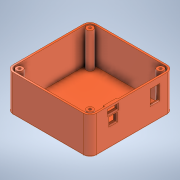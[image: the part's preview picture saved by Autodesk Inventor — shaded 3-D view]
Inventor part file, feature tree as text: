
AUTODESK INVENTOR PART (.ipt)
format: ipt  version: 2020 (Build 240168000, 168)  size: 254,464 bytes
history: native  units: in
note: dims shown in document units (in); Inventor stores cm internally (conversion verified against a paired STEP export)
features: extrude x6, sketch x6, projected_geometry x5, mirror x2, chamfer x2, shell x1, fillet x1
ambient origin geometry x8: Origin, YZ Plane, XZ Plane, XY Plane, X Axis, Y Axis, Z Axis, Center Point
bodies: Solid1 (feature_tree)
feature tree (23):
  extrude  "Extrusion1"  Depth=3.1496in
  shell  "Shell1"  Thickness=0.25in
  fillet  "Fillet1"  Radius=1.0in
  extrude  "Extrusion2"  Depth=0.05in
  mirror  "Mirror1"
  mirror  "Mirror2"
  extrude  "Extrusion4"  Depth=0.25in
  extrude  "Extrusion5"  Depth=0.3937in TaperAngle=0.0deg
  extrude  "Extrusion6"  Depth=0.5in
  chamfer  "Chamfer1"  Distance=0.3937in
  extrude  "Extrusion7"  Depth=0.1575in
  chamfer  "Chamfer2"  Distance=0.0689in
  sketch  "Sketch1"  dims[d0=3.1496in d1=3.1496in d2=0.25in d3=1.0in d4=0.0in]
  sketch  "Sketch2"  dims[d5=0.0669in d6=0.05in]
  sketch  "Sketch4"  dims[d7=0.25in d8=0.0945in]
  projected_geometry  "Projected Loop1"
  projected_geometry  "Projected Loop2"
  projected_geometry  "Projected Loop3"
  projected_geometry  "Projected Loop4"
  projected_geometry  "Projected Loop5"
  sketch  "Sketch5"  dims[d9=1.0in d10=0.0in d16=0.3937in d17=0.0in]
  sketch  "Sketch6"  dims[d18=0.05in d19=0.5in d20=0.3937in d21=0.0in]
  sketch  "Sketch7"  dims[d22=0.3543in d23=0.1575in d24=0.0689in d25=0.1181in d26=0.252in d27=0.252in d28=0.1181in d29=0.3937in d30=0.0in d31=0.0394in d32=0.125in d33=45.0deg d34=0.31in d35=0.51in d36=0.25in d37=0.3in d38=1.0in d39=0.0in d40=0.03in d41=0.125in d42=45.0deg]
